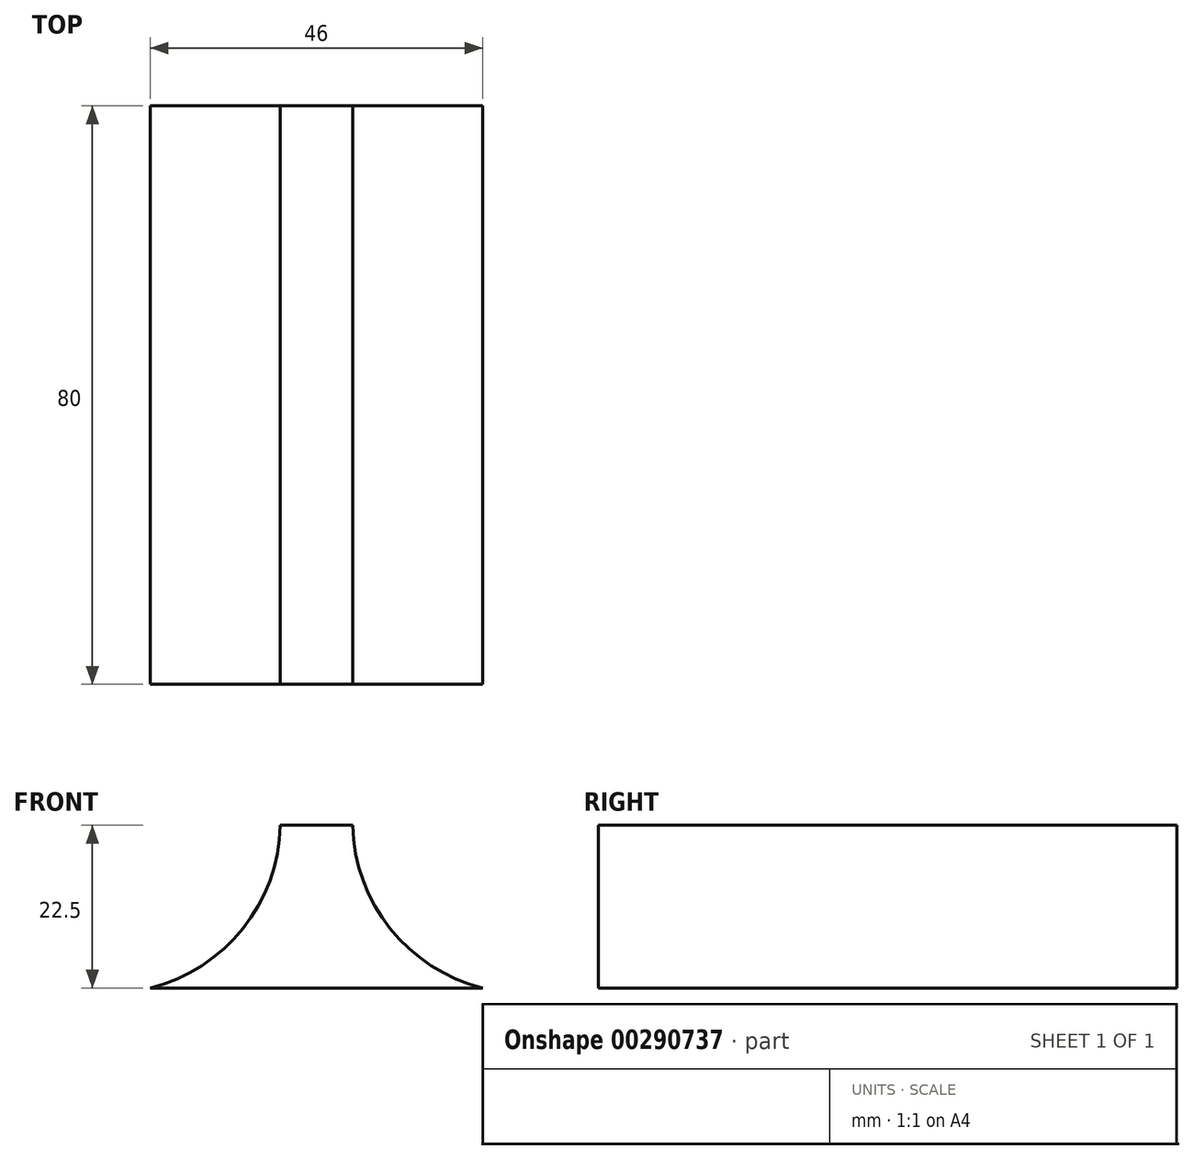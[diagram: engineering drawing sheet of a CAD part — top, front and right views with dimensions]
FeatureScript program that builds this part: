
annotation { "Feature Type Name" : "Feature", "Feature Type Description" : "" }
export const myFeature = defineFeature(function(context is Context, id is Id, definition is map)
    precondition{}
    {
        {
            var Q0;
            Q0=qCreatedBy(makeId("Front.planeOp"),FACE);
            var sketch = newSketch(context, id + "F0", { "sketchPlane" : qUnion([Q0])});
            skLineSegment(sketch, "E0", {"start": v(0, -25) * mm, "end": v(23, -25) * mm});
            skLineSegment(sketch, "E1", {"start": v(0, -25) * mm, "end": v(0, -2.5) * mm});
            skLineSegment(sketch, "E2", {"start": v(0, -2.5) * mm, "end": v(5, -2.5) * mm});
            skArc(sketch, "E3", {"start": v(5, -2.5) * mm, "mid": v(10.19, -16.8) * mm, "end": v(23, -25) * mm});
            skSolve(sketch);
        }
        {
            var Q0;
            Q0=makeQuery(id+"F0.imprint","IMPRINT",FACE,{"disambiguationData":[TD([[makeQuery(id+"F0.imprint","IMPRINT",EDGE,{"derivedFrom":sQuery(id+"F0.wireOp",EDGE,"E0")}),1.0]])]});
            extrude(context, id + "F1", {"entities" : qUnion([Q0]), "depth" : 80 * mm});
        }
        {
            var Q0;
            Q0=makeQuery(id+"F1.opExtrude","SWEPT_BODY",BODY,{"disambiguationData":[OSD([sQuery(id+"F0.wireOp",EDGE,"E0"),sQuery(id+"F0.wireOp",EDGE,"E1"),sQuery(id+"F0.wireOp",EDGE,"Z2qvNqBz-pLLF-02rl-ZM0D-pI5LhpRe7Agh"),sQuery(id+"F0.wireOp",EDGE,"UT41Hp6Y-dT08-Xopo-x3i4-KngJXu6tiJp2"),sQuery(id+"F0.wireOp",EDGE,"OkGFd4dK-1NLV-PATP-nztZ-qypUdjQCxw63"),sQuery(id+"F0.wireOp",EDGE,"sFPqD9eX-AXz5-Ktwp-ukWW-KThPlENJ3f0R")])]});
            var Q1;
            Q1=qCreatedBy(makeId("Right.planeOp"),FACE);
            mirror(context, id + "F2", {"operationType" : NewBodyOperationType.ADD, "entities" : qUnion([Q0]), "mirrorPlane" : qUnion([Q1])});
        }
    });
